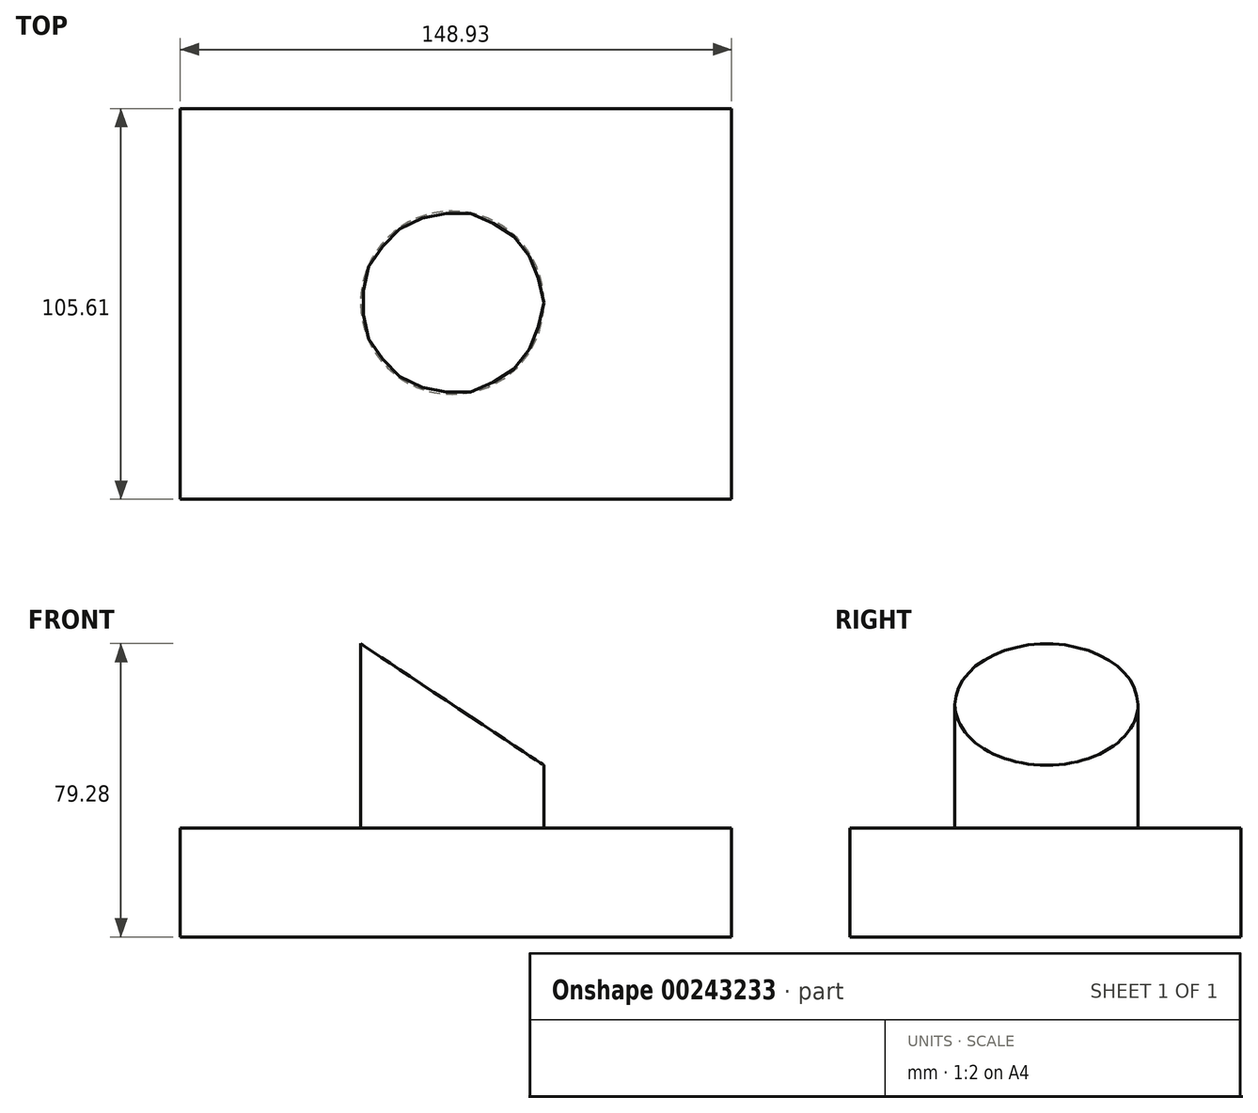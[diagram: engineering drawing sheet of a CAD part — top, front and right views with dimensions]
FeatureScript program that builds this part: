
annotation { "Feature Type Name" : "Feature", "Feature Type Description" : "" }
export const myFeature = defineFeature(function(context is Context, id is Id, definition is map)
    precondition{}
    {
        {
            var Q0;
            Q0=qCreatedBy(makeId("Top.planeOp"),FACE);
            var sketch = newSketch(context, id + "F0", { "sketchPlane" : qUnion([Q0])});
            skLineSegment(sketch, "E0", {"start": v(-57.89, -47.34) * mm, "end": v(-57.89, 58.27) * mm});
            skLineSegment(sketch, "E1", {"start": v(-57.89, 58.27) * mm, "end": v(91.04, 58.27) * mm});
            skLineSegment(sketch, "E2", {"start": v(91.04, -47.34) * mm, "end": v(91.04, 58.27) * mm});
            skLineSegment(sketch, "E3", {"start": v(-57.89, -47.34) * mm, "end": v(91.04, -47.34) * mm});
            skSolve(sketch);
        }
        {
            var Q0;
            Q0=makeQuery(id+"F0.imprint","IMPRINT",FACE,{"disambiguationData":[TD([[makeQuery(id+"F0.imprint","IMPRINT",EDGE,{"derivedFrom":sQuery(id+"F0.wireOp",EDGE,"E0")}),-1.0]])]});
            extrude(context, id + "F1", {"entities" : qUnion([Q0]), "depth" : 29.46 * mm});
        }
        {
            var Q0;
            Q0=makeQuery(id+"F1.opExtrude","CAP_FACE",FACE,{"disambiguationData":[OSD([sQuery(id+"F0.wireOp",EDGE,"E0"),sQuery(id+"F0.wireOp",EDGE,"E1"),sQuery(id+"F0.wireOp",EDGE,"E2"),sQuery(id+"F0.wireOp",EDGE,"E3")])],"isStart":false});
            var sketch = newSketch(context, id + "F2", { "sketchPlane" : qUnion([Q0])});
            skCircle(sketch, "E4", {"center": v(15.58, 5.79) * mm, "radius": 24.77 * mm});
            skSolve(sketch);
        }
        {
            var Q0;
            Q0=makeQuery(id+"F2.imprint","IMPRINT",FACE,{"disambiguationData":[TD([[makeQuery(id+"F2.imprint","IMPRINT",EDGE,{"derivedFrom":sQuery(id+"F2.wireOp",EDGE,"E4")}),1.0]])]});
            extrude(context, id + "F3", {"entities" : qUnion([Q0]), "operationType" : NewBodyOperationType.ADD, "depth" : 51.3 * mm});
        }
        {
            var Q0;
            Q0=qCreatedBy(makeId("Front.planeOp"),FACE);
            var sketch = newSketch(context, id + "F4", { "sketchPlane" : qUnion([Q0])});
            skLineSegment(sketch, "E5.bottom", {"start": v(-16.46, 84.1) * mm, "end": v(40.66, 84.1) * mm});
            skLineSegment(sketch, "E5.right", {"start": v(40.66, 84.1) * mm, "end": v(40.66, 46.18) * mm});
            skLineSegment(sketch, "E6", {"start": v(-16.46, 84.1) * mm, "end": v(40.66, 46.18) * mm});
            skSolve(sketch);
        }
        {
            var Q0;
            Q0 = qSketchRegion(id + "F4", true);
            extrude(context, id + "F5", {"entities" : qUnion([Q0]), "operationType" : NewBodyOperationType.REMOVE, "endBound" : BoundingType.SYMMETRIC, "oppositeDirection" : true, "depth" : 2286 * mm});
        }
    });
